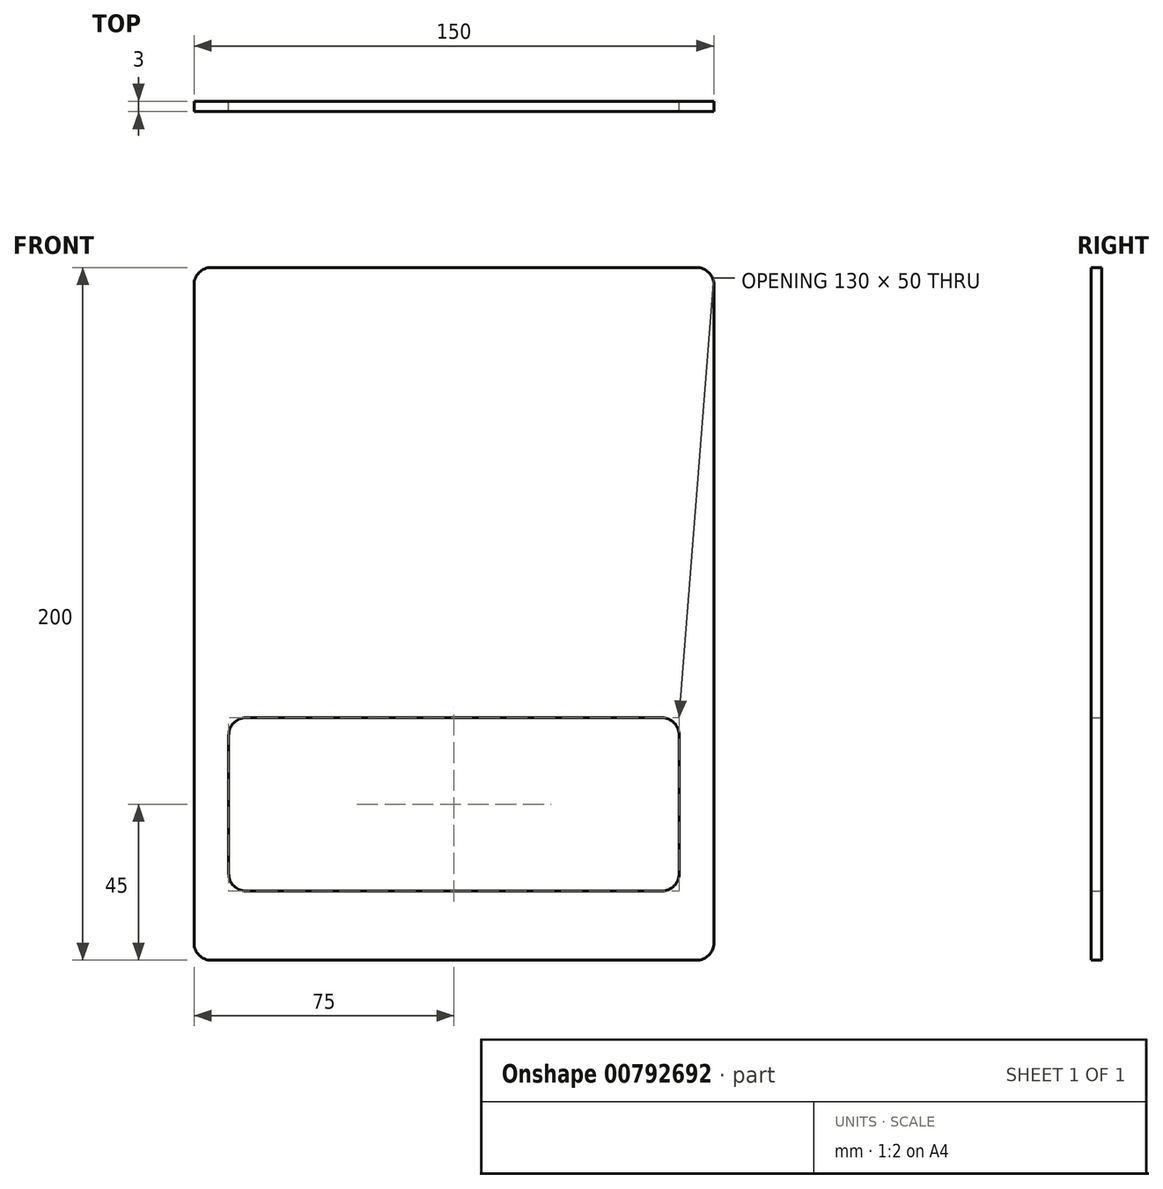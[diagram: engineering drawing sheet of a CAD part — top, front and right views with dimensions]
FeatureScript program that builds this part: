
annotation { "Feature Type Name" : "Feature", "Feature Type Description" : "" }
export const myFeature = defineFeature(function(context is Context, id is Id, definition is map)
    precondition{}
    {
        {
            var Q0;
            Q0=qCreatedBy(makeId("Front.planeOp"),FACE);
            var sketch = newSketch(context, id + "F0", { "sketchPlane" : qUnion([Q0])});
            skLineSegment(sketch, "E0.bottom", {"start": v(-70, 100) * mm, "end": v(70, 100) * mm});
            skLineSegment(sketch, "E0.top", {"start": v(-70, -100) * mm, "end": v(70, -100) * mm});
            skLineSegment(sketch, "E0.left", {"start": v(-75, 95) * mm, "end": v(-75, -95) * mm});
            skLineSegment(sketch, "E0.right", {"start": v(75, 95) * mm, "end": v(75, -95) * mm});
            skLineSegment(sketch, "E1.bottom", {"start": v(-60, -30) * mm, "end": v(60, -30) * mm});
            skLineSegment(sketch, "E1.top", {"start": v(-60, -80) * mm, "end": v(60, -80) * mm});
            skLineSegment(sketch, "E1.left", {"start": v(-65, -35) * mm, "end": v(-65, -75) * mm});
            skLineSegment(sketch, "E1.right", {"start": v(65, -35) * mm, "end": v(65, -75) * mm});
            skPoint(sketch, "E2.visualSharp", {"position": v(-75, 100) * mm});
            skArc(sketch, "E2.filletArc", {"start": v(-70, 100) * mm, "mid": v(-73.54, 98.54) * mm, "end": v(-75, 95) * mm});
            skPoint(sketch, "E3.visualSharp", {"position": v(75, 100) * mm});
            skArc(sketch, "E3.filletArc", {"start": v(75, 95) * mm, "mid": v(73.54, 98.54) * mm, "end": v(70, 100) * mm});
            skPoint(sketch, "E4.visualSharp", {"position": v(-65, -30) * mm});
            skArc(sketch, "E4.filletArc", {"start": v(-60, -30) * mm, "mid": v(-63.54, -31.46) * mm, "end": v(-65, -35) * mm});
            skPoint(sketch, "E5.visualSharp", {"position": v(65, -30) * mm});
            skArc(sketch, "E5.filletArc", {"start": v(65, -35) * mm, "mid": v(63.54, -31.46) * mm, "end": v(60, -30) * mm});
            skPoint(sketch, "E6.visualSharp", {"position": v(65, -80) * mm});
            skArc(sketch, "E6.filletArc", {"start": v(60, -80) * mm, "mid": v(63.54, -78.54) * mm, "end": v(65, -75) * mm});
            skPoint(sketch, "E7.visualSharp", {"position": v(-65, -80) * mm});
            skArc(sketch, "E7.filletArc", {"start": v(-65, -75) * mm, "mid": v(-63.54, -78.54) * mm, "end": v(-60, -80) * mm});
            skPoint(sketch, "E8.visualSharp", {"position": v(-75, -100) * mm});
            skArc(sketch, "E8.filletArc", {"start": v(-75, -95) * mm, "mid": v(-73.54, -98.54) * mm, "end": v(-70, -100) * mm});
            skPoint(sketch, "E9.visualSharp", {"position": v(75, -100) * mm});
            skArc(sketch, "E9.filletArc", {"start": v(70, -100) * mm, "mid": v(73.54, -98.54) * mm, "end": v(75, -95) * mm});
            skSolve(sketch);
        }
        {
            var Q0;
            Q0=makeQuery(id+"F0.imprint","IMPRINT",FACE,{"disambiguationData":[TD([[makeQuery(id+"F0.imprint","IMPRINT",EDGE,{"derivedFrom":sQuery(id+"F0.wireOp",EDGE,"E0.bottom")}),-1.0]])]});
            var Q1;
            Q1 = qSketchRegion(id + "F0", true);
            extrude(context, id + "F1", {"entities" : qUnion([Q0, Q1]), "depth" : 3 * mm, "offsetDistance" : 25 * mm});
        }
    });
